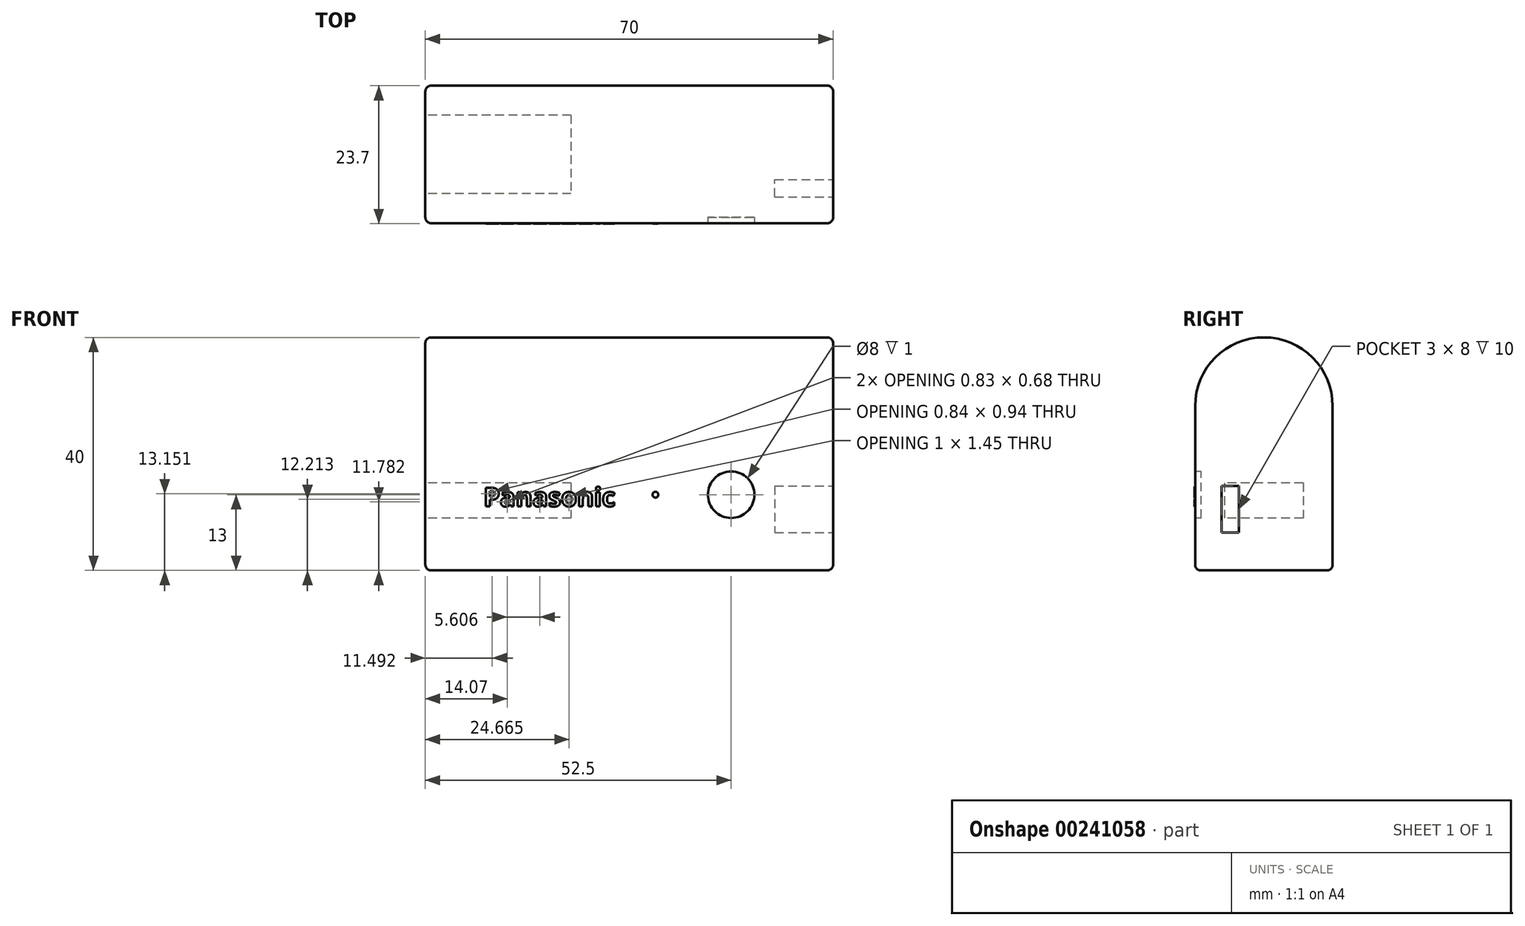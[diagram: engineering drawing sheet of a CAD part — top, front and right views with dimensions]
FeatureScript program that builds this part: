
annotation { "Feature Type Name" : "Feature", "Feature Type Description" : "" }
export const myFeature = defineFeature(function(context is Context, id is Id, definition is map)
    precondition{}
    {
        {
            var Q0;
            Q0=qCreatedBy(makeId("Right.planeOp"),FACE);
            var sketch = newSketch(context, id + "F0", { "sketchPlane" : qUnion([Q0])});
            skLineSegment(sketch, "E0.bottom", {"start": v(-11.8, 28.2) * mm, "end": v(11.8, 28.2) * mm});
            skLineSegment(sketch, "E0.top", {"start": v(-11.8, 0) * mm, "end": v(11.8, 0) * mm});
            skLineSegment(sketch, "E0.left", {"start": v(-11.8, 28.2) * mm, "end": v(-11.8, 0) * mm});
            skLineSegment(sketch, "E0.right", {"start": v(11.8, 28.2) * mm, "end": v(11.8, 0) * mm});
            skPoint(sketch, "E1", {"position": v(0, 0) * mm});
            skArc(sketch, "E2", {"start": v(11.8, 28.2) * mm, "mid": v(0, 40) * mm, "end": v(-11.8, 28.2) * mm});
            skSolve(sketch);
        }
        {
            var Q0;
            Q0=makeQuery(id+"F0.imprint","IMPRINT",FACE,{"disambiguationData":[TD([[makeQuery(id+"F0.imprint","IMPRINT",EDGE,{"derivedFrom":sQuery(id+"F0.wireOp",EDGE,"E0.bottom")}),-1.0]])]});
            var Q1;
            Q1=makeQuery(id+"F0.imprint","IMPRINT",FACE,{"disambiguationData":[TD([[makeQuery(id+"F0.imprint","IMPRINT",EDGE,{"derivedFrom":sQuery(id+"F0.wireOp",EDGE,"E0.bottom")}),1.0]])]});
            extrude(context, id + "F1", {"entities" : qUnion([Q0, Q1]), "endBound" : BoundingType.SYMMETRIC, "depth" : 70 * mm});
        }
        {
            var Q0;
            Q0=makeQuery(id+"F1.opExtrude","SWEPT_FACE",FACE,{"disambiguationData":[OSD([sQuery(id+"F0.wireOp",EDGE,"E0.left")])]});
            var sketch = newSketch(context, id + "F2", { "sketchPlane" : qUnion([Q0])});
            skText(sketch, "E3", { "text": "Panasonic", "fontName": "OpenSans-Bold.ttf"});
            const initialGuessF2  = {"E3": [-0.025, 0.011, 1, 0, 0.0032]};
            skSetInitialGuess(sketch, initialGuessF2);
            skSolve(sketch);
        }
        {
            var Q0;
            Q0 = qSketchRegion(id + "F2", true);
            extrude(context, id + "F3", {"entities" : qUnion([Q0]), "depth" : 0.1 * mm});
        }
        {
            var Q0;
            Q0=makeQuery(id+"F1.opExtrude","SWEPT_FACE",FACE,{"disambiguationData":[OSD([sQuery(id+"F0.wireOp",EDGE,"E0.left")])]});
            var sketch = newSketch(context, id + "F4", { "sketchPlane" : qUnion([Q0])});
            skCircle(sketch, "E4", {"center": v(17.5, 13) * mm, "radius": 4 * mm});
            skSolve(sketch);
        }
        {
            var Q0;
            Q0=makeQuery(id+"F4.imprint","IMPRINT",FACE,{"disambiguationData":[TD([[makeQuery(id+"F4.imprint","IMPRINT",EDGE,{"derivedFrom":sQuery(id+"F4.wireOp",EDGE,"E4")}),1.0]])]});
            extrude(context, id + "F5", {"entities" : qUnion([Q0]), "operationType" : NewBodyOperationType.REMOVE, "oppositeDirection" : true, "depth" : 1 * mm});
        }
        {
            var Q0;
            Q0=makeQuery(id+"F1.opExtrude","CAP_FACE",FACE,{"disambiguationData":[OSD([sQuery(id+"F0.wireOp",EDGE,"E0.top"),sQuery(id+"F0.wireOp",EDGE,"E0.left"),sQuery(id+"F0.wireOp",EDGE,"E0.right"),sQuery(id+"F0.wireOp",EDGE,"E2")])],"isStart":true});
            var sketch = newSketch(context, id + "F6", { "sketchPlane" : qUnion([Q0])});
            skLineSegment(sketch, "E5.bottom", {"start": v(-6.75, 15) * mm, "end": v(6.75, 15) * mm});
            skLineSegment(sketch, "E5.top", {"start": v(-6.75, 9) * mm, "end": v(6.75, 9) * mm});
            skLineSegment(sketch, "E5.left", {"start": v(-6.75, 15) * mm, "end": v(-6.75, 9) * mm});
            skLineSegment(sketch, "E5.right", {"start": v(6.75, 15) * mm, "end": v(6.75, 9) * mm});
            skPoint(sketch, "E6", {"position": v(0, 9) * mm});
            skPoint(sketch, "E7", {"position": v(0, 0) * mm});
            skSolve(sketch);
        }
        {
            var Q0;
            Q0=makeQuery(id+"F6.imprint","IMPRINT",FACE,{"disambiguationData":[TD([[makeQuery(id+"F6.imprint","IMPRINT",EDGE,{"derivedFrom":sQuery(id+"F6.wireOp",EDGE,"E5.bottom")}),-1.0]])]});
            extrude(context, id + "F7", {"entities" : qUnion([Q0]), "operationType" : NewBodyOperationType.REMOVE, "oppositeDirection" : true, "depth" : 25 * mm});
        }
        {
            var Q0;
            Q0=makeQuery(id+"F1.opExtrude","CAP_FACE",FACE,{"disambiguationData":[OSD([sQuery(id+"F0.wireOp",EDGE,"E0.top"),sQuery(id+"F0.wireOp",EDGE,"E0.left"),sQuery(id+"F0.wireOp",EDGE,"E0.right"),sQuery(id+"F0.wireOp",EDGE,"E2")])],"isStart":false});
            var sketch = newSketch(context, id + "F8", { "sketchPlane" : qUnion([Q0])});
            skLineSegment(sketch, "E8.bottom", {"start": v(-7.3, 14.5) * mm, "end": v(-4.3, 14.5) * mm});
            skLineSegment(sketch, "E8.top", {"start": v(-7.3, 6.5) * mm, "end": v(-4.3, 6.5) * mm});
            skLineSegment(sketch, "E8.left", {"start": v(-7.3, 14.5) * mm, "end": v(-7.3, 6.5) * mm});
            skLineSegment(sketch, "E8.right", {"start": v(-4.3, 14.5) * mm, "end": v(-4.3, 6.5) * mm});
            skSolve(sketch);
        }
        {
            var Q0;
            Q0=makeQuery(id+"F8.imprint","IMPRINT",FACE,{"disambiguationData":[TD([[makeQuery(id+"F8.imprint","IMPRINT",EDGE,{"derivedFrom":sQuery(id+"F8.wireOp",EDGE,"E8.bottom")}),-1.0]])]});
            extrude(context, id + "F9", {"entities" : qUnion([Q0]), "operationType" : NewBodyOperationType.REMOVE, "oppositeDirection" : true, "depth" : 10 * mm});
        }
        {
            var Q0;
            Q0=makeQuery(id+"F1.opExtrude","SWEPT_EDGE",EDGE,{"disambiguationData":[OSD([sQuery(id+"F0.wireOp",EDGE,"E0.top"),sQuery(id+"F0.wireOp",EDGE,"E0.left")])]});
            var Q1;
            Q1=makeQuery(id+"F1.opExtrude","CAP_EDGE",EDGE,{"disambiguationData":[OSD([sQuery(id+"F0.wireOp",EDGE,"E0.top")])],"isStart":true});
            var Q2;
            Q2=makeQuery(id+"F1.opExtrude","SWEPT_EDGE",EDGE,{"disambiguationData":[OSD([sQuery(id+"F0.wireOp",EDGE,"E0.top"),sQuery(id+"F0.wireOp",EDGE,"E0.right")])]});
            var Q3;
            Q3=makeQuery(id+"F1.opExtrude","CAP_EDGE",EDGE,{"disambiguationData":[OSD([sQuery(id+"F0.wireOp",EDGE,"E0.top")])],"isStart":false});
            var Q4;
            Q4=makeQuery(id+"F1.opExtrude","CAP_EDGE",EDGE,{"disambiguationData":[OSD([sQuery(id+"F0.wireOp",EDGE,"E0.left")])],"isStart":true});
            var Q5;
            Q5=makeQuery(id+"F1.opExtrude","CAP_EDGE",EDGE,{"disambiguationData":[OSD([sQuery(id+"F0.wireOp",EDGE,"E0.right")])],"isStart":true});
            var Q6;
            Q6=makeQuery(id+"F1.opExtrude","CAP_EDGE",EDGE,{"disambiguationData":[OSD([sQuery(id+"F0.wireOp",EDGE,"E0.left")])],"isStart":false});
            var Q7;
            Q7=makeQuery(id+"F1.opExtrude","CAP_EDGE",EDGE,{"disambiguationData":[OSD([sQuery(id+"F0.wireOp",EDGE,"E0.right")])],"isStart":false});
            var Q8;
            Q8=makeQuery(id+"F1.opExtrude","CAP_EDGE",EDGE,{"disambiguationData":[OSD([sQuery(id+"F0.wireOp",EDGE,"E2")])],"isStart":false});
            var Q9;
            Q9=makeQuery(id+"F1.opExtrude","CAP_EDGE",EDGE,{"disambiguationData":[OSD([sQuery(id+"F0.wireOp",EDGE,"E2")])],"isStart":true});
            fillet(context, id + "F10", {"entities" : qUnion([Q0, Q1, Q2, Q3, Q4, Q5, Q6, Q7, Q8, Q9]), "radius" : 1 * mm, "tangentPropagation" : true, "allowEdgeOverflow" : false});
        }
        {
            var Q0;
            Q0=makeQuery(id+"F1.opExtrude","SWEPT_FACE",FACE,{"disambiguationData":[OSD([sQuery(id+"F0.wireOp",EDGE,"E0.left")])]});
            var sketch = newSketch(context, id + "F11", { "sketchPlane" : qUnion([Q0])});
            skCircle(sketch, "E9", {"center": v(4.5, 13) * mm, "radius": 0.5 * mm});
            skPoint(sketch, "E10", {"position": v(17.5, 13) * mm});
            skSolve(sketch);
        }
        {
            var Q0;
            Q0=makeQuery(id+"F11.imprint","IMPRINT",FACE,{"disambiguationData":[TD([[makeQuery(id+"F11.imprint","IMPRINT",EDGE,{"derivedFrom":sQuery(id+"F11.wireOp",EDGE,"E9")}),1.0]])]});
            extrude(context, id + "F12", {"entities" : qUnion([Q0]), "depth" : 0.1 * mm});
        }
    });
